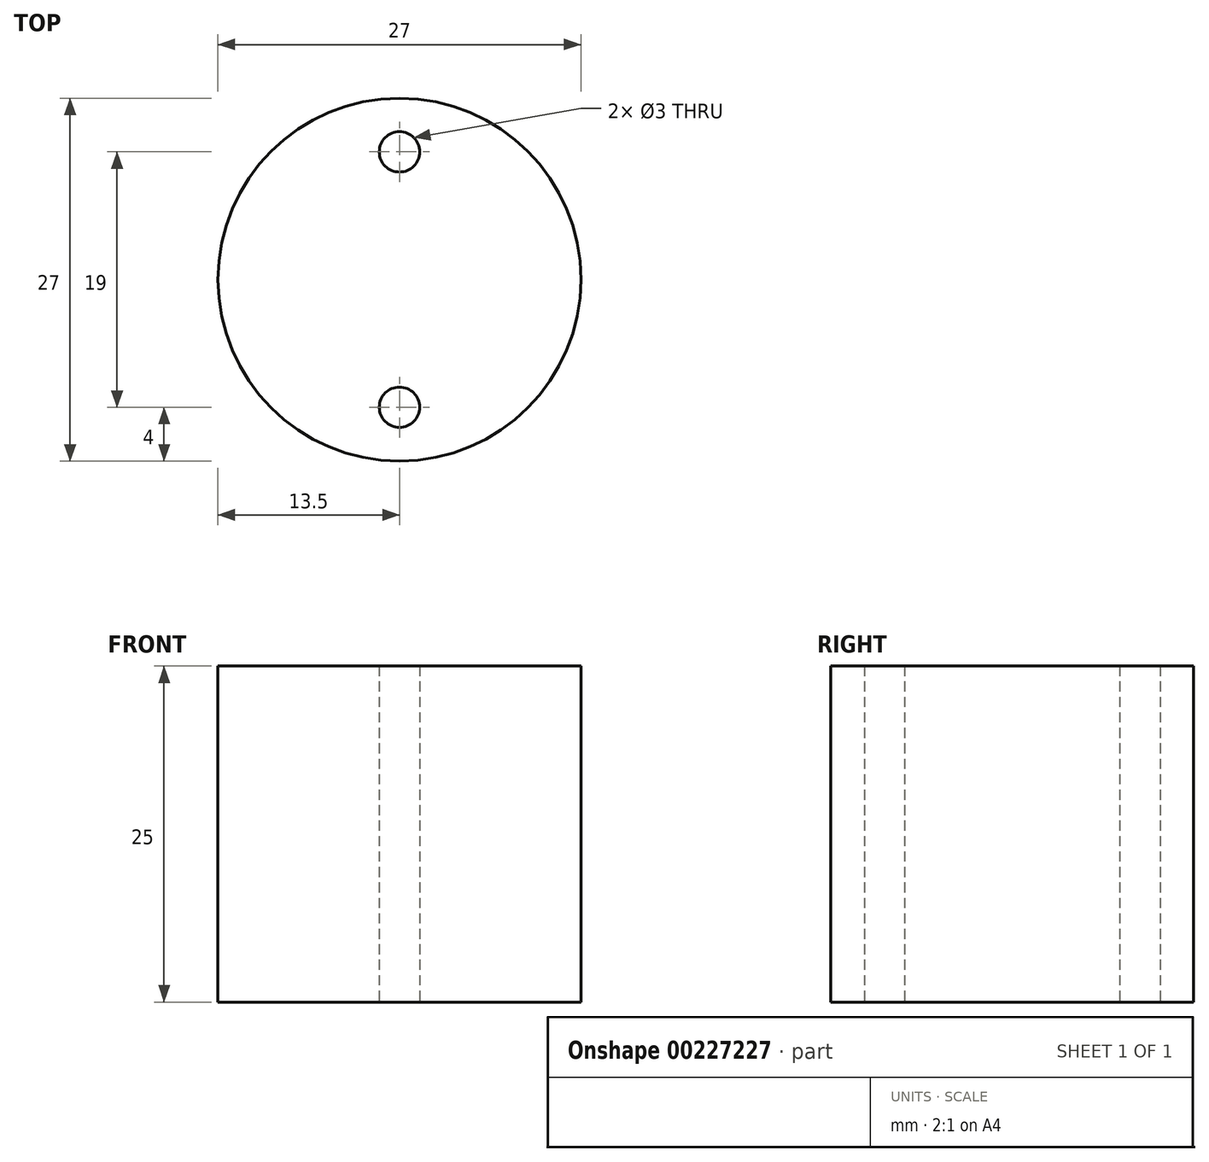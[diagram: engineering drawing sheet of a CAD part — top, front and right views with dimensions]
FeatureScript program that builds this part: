
annotation { "Feature Type Name" : "Feature", "Feature Type Description" : "" }
export const myFeature = defineFeature(function(context is Context, id is Id, definition is map)
    precondition{}
    {
        {
            var Q0;
            Q0=qCreatedBy(makeId("Top.planeOp"),FACE);
            var sketch = newSketch(context, id + "F0", { "sketchPlane" : qUnion([Q0])});
            skCircle(sketch, "E0", {"center": v(0, 0) * mm, "radius": 13.5 * mm});
            skCircle(sketch, "E1", {"center": v(0, 9.5) * mm, "radius": 1.5 * mm});
            skCircle(sketch, "E2", {"center": v(0, -9.5) * mm, "radius": 1.5 * mm});
            skSolve(sketch);
        }
        {
            var Q0;
            Q0 = qSketchRegion(id + "F0", true);
            extrude(context, id + "F1", {"entities" : qUnion([Q0]), "depth" : 25 * mm});
        }
    });
